# Revit family: LCC6LED-W
name_source: partatom
category: Lighting Fixtures
revit_build: Autodesk Revit MEP 2012 (Build: 20110916_2132(x64)
units: mm (PartAtom-declared; Revit-internal decimal feet)

## types (4) — shared parameters
Apparent Load = 40 VA
Backbox = Hubbell - Matt Black
Color Filter = 16777215
Default Elevation = 48.000"
Description = 6in LED Wall Mount Cylinder
Dimming Lamp Color Temperature Shift = <None>
Emit Shape Visible in Rendering = No
Emit from Circle Diameter = 5.500"
Glass = Hubbell - White Glass
Is 120V = Yes
Is 277V = No
Lamp = LED Lamp
Load Classification = Lighting
Manufacturer = Prescolite
Manufacturer Fax = 864-678-1415
Model = LCC6LED
Product Documentation Link = http://cdn.prescolite.com
Product Page URL = http://www.prescolite.com
Tilt Angle = 90.00°
URL = http://www.prescolite.com
Voltage = 120 V
Wattage Comments = 40W

## per-type parameters (varying)
| type | Photometric Web File |
| LCC6LEDV2S24L30K8WWBL | LCC6LEDV2S24L30K8WWBL.IES |
| LCC6LEDV2S24L35K8WFL45BL | LCC6LEDV2S24L35K8WFL45BL.IES |
| LCC6LEDV2S30L30K8WWBL | LCC6LEDV2S30L30K8WWBL.IES |
| LCC6LEDV2S30L35K8WFL45BL | LCC6LEDV2S30L35K8WFL45BL.IES |

## geometry (parser evidence)
native form markers: Blend x1, Sweep x1
no freeform markers — native parametric forms only
